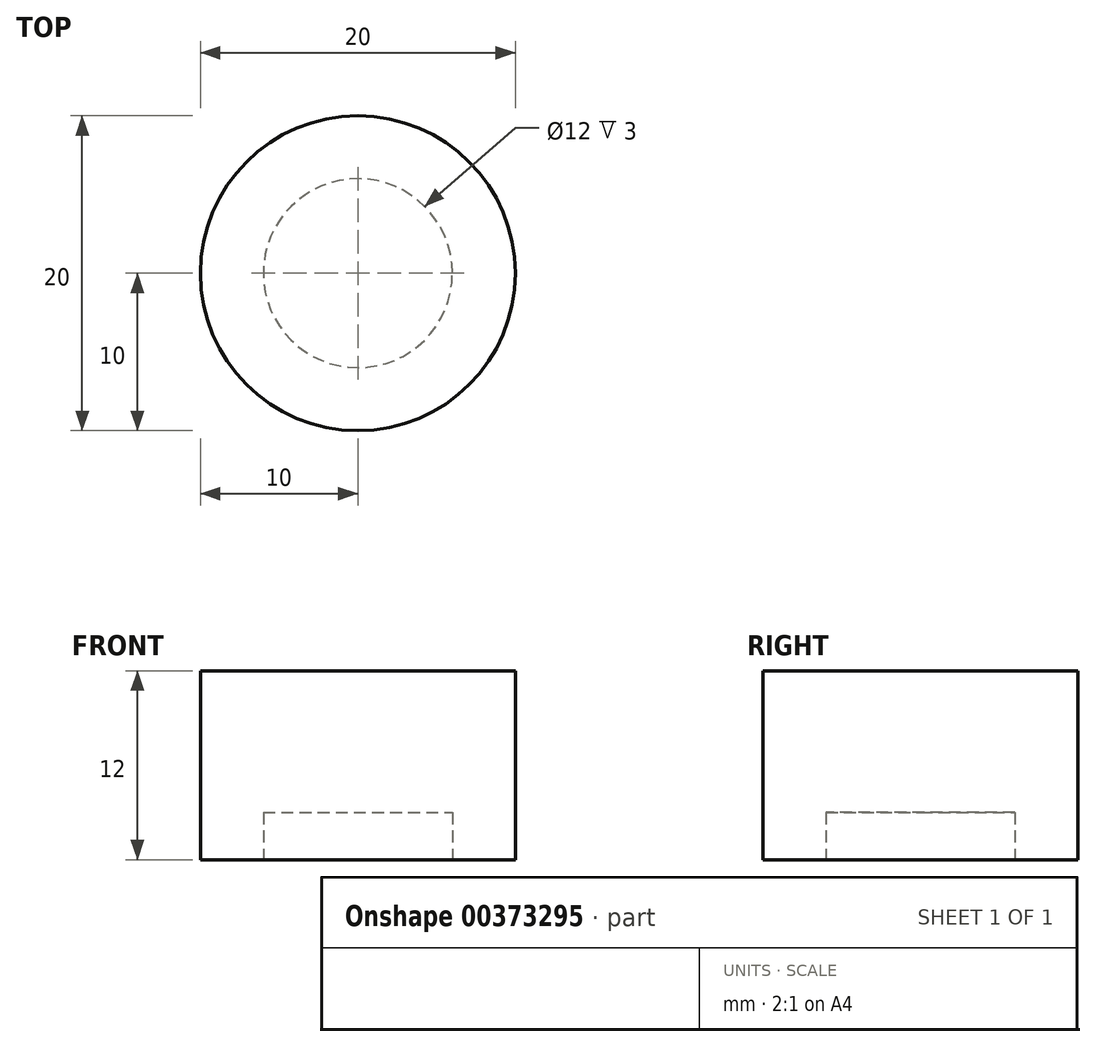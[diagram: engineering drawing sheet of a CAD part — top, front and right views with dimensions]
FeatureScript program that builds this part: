
annotation { "Feature Type Name" : "Feature", "Feature Type Description" : "" }
export const myFeature = defineFeature(function(context is Context, id is Id, definition is map)
    precondition{}
    {
        {
            var Q0;
            Q0=qCreatedBy(makeId("Top.planeOp"),FACE);
            var sketch = newSketch(context, id + "F0", { "sketchPlane" : qUnion([Q0])});
            skCircle(sketch, "E0", {"center": v(0, 0) * mm, "radius": 10 * mm});
            skSolve(sketch);
        }
        {
            var Q0;
            Q0=makeQuery(id+"F0.imprint","IMPRINT",FACE,{"disambiguationData":[TD([[makeQuery(id+"F0.imprint","IMPRINT",EDGE,{"derivedFrom":sQuery(id+"F0.wireOp",EDGE,"E0")}),1.0]])]});
            extrude(context, id + "F1", {"entities" : qUnion([Q0]), "depth" : 12 * mm, "offsetDistance" : 25.4 * mm});
        }
        {
            var Q0;
            Q0=makeQuery(id+"F1.opExtrude","CAP_FACE",FACE,{"disambiguationData":[OSD([sQuery(id+"F0.wireOp",EDGE,"E0")])],"isStart":true});
            var sketch = newSketch(context, id + "F2", { "sketchPlane" : qUnion([Q0])});
            skCircle(sketch, "E1", {"center": v(0, 0) * mm, "radius": 6 * mm});
            skSolve(sketch);
        }
        {
            var Q0;
            Q0=makeQuery(id+"F2.imprint","IMPRINT",FACE,{"disambiguationData":[TD([[makeQuery(id+"F2.imprint","IMPRINT",EDGE,{"derivedFrom":sQuery(id+"F2.wireOp",EDGE,"E1")}),1.0]])]});
            extrude(context, id + "F3", {"entities" : qUnion([Q0]), "operationType" : NewBodyOperationType.REMOVE, "oppositeDirection" : true, "depth" : 3 * mm, "offsetDistance" : 25.4 * mm});
        }
    });
